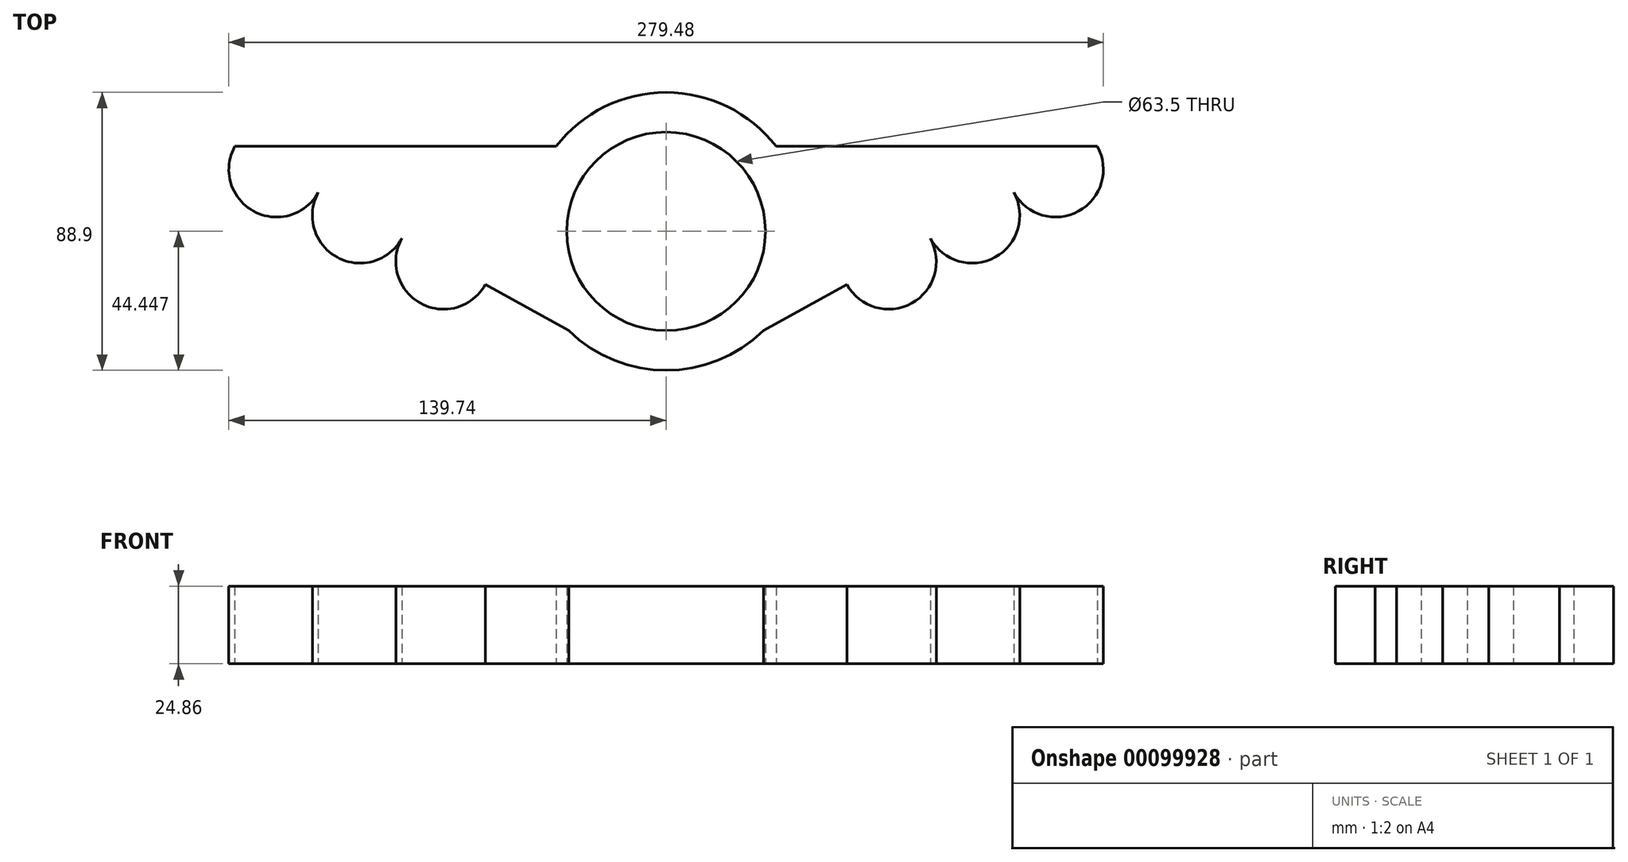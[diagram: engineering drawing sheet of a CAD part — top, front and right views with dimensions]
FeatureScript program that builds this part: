
annotation { "Feature Type Name" : "Feature", "Feature Type Description" : "" }
export const myFeature = defineFeature(function(context is Context, id is Id, definition is map)
    precondition{}
    {
        {
            var Q0;
            Q0=qCreatedBy(makeId("Top.planeOp"),FACE);
            var sketch = newSketch(context, id + "F0", { "sketchPlane" : qUnion([Q0])});
            skCircle(sketch, "E0", {"center": v(0, -31.71) * mm, "radius": 44.45 * mm});
            skCircle(sketch, "E1", {"center": v(0, -31.71) * mm, "radius": 31.75 * mm});
            skLineSegment(sketch, "E2", {"start": v(0, -31.71) * mm, "end": v(44.45, -31.71) * mm});
            skLineSegment(sketch, "E3", {"start": v(44.45, -31.71) * mm, "end": v(44.45, 0) * mm});
            skLineSegment(sketch, "E4", {"start": v(44.45, 0) * mm, "end": v(0, 0) * mm});
            skLineSegment(sketch, "E5", {"start": v(44.45, 0) * mm, "end": v(146.05, 0) * mm});
            skLineSegment(sketch, "E6", {"start": v(0, -63.46) * mm, "end": v(44.45, -63.46) * mm});
            skLineSegment(sketch, "E7", {"start": v(44.45, -31.71) * mm, "end": v(44.45, -63.46) * mm});
            skLineSegment(sketch, "E8", {"start": v(31.1, -63.46) * mm, "end": v(146.05, 0) * mm});
            skCircle(sketch, "E9", {"center": v(44.45, -56.1) * mm, "radius": 15.24 * mm});
            skCircle(sketch, "E10", {"center": v(71.13, -41.36) * mm, "radius": 15.24 * mm});
            skCircle(sketch, "E11", {"center": v(97.82, -26.63) * mm, "radius": 15.24 * mm});
            skCircle(sketch, "E12", {"center": v(124.5, -11.9) * mm, "radius": 15.24 * mm});
            skLineSegment(sketch, "E13", {"start": v(137.84, -4.53) * mm, "end": v(35.17, -4.53) * mm});
            skLineSegment(sketch, "E14", {"start": v(0, -31.71) * mm, "end": v(-44.45, -31.71) * mm});
            skLineSegment(sketch, "E15", {"start": v(0, 0) * mm, "end": v(-44.45, 0) * mm});
            skLineSegment(sketch, "E16", {"start": v(-44.45, 0) * mm, "end": v(-146.05, 0) * mm});
            skLineSegment(sketch, "E17", {"start": v(-44.45, -31.71) * mm, "end": v(-44.45, -63.46) * mm});
            skLineSegment(sketch, "E18", {"start": v(0, -63.46) * mm, "end": v(-44.45, -63.46) * mm});
            skLineSegment(sketch, "E19", {"start": v(-31.1, -63.46) * mm, "end": v(-146.05, 0) * mm});
            skCircle(sketch, "E20", {"center": v(-44.45, -56.1) * mm, "radius": 15.24 * mm});
            skCircle(sketch, "E21", {"center": v(-71.13, -41.36) * mm, "radius": 15.24 * mm});
            skCircle(sketch, "E22", {"center": v(-97.82, -26.63) * mm, "radius": 15.24 * mm});
            skCircle(sketch, "E23", {"center": v(-124.5, -11.9) * mm, "radius": 15.24 * mm});
            skLineSegment(sketch, "E24", {"start": v(-137.84, -4.53) * mm, "end": v(-35.17, -4.53) * mm});
            skSolve(sketch);
        }
        {
            var Q0;
            Q0=makeQuery(id+"F0.imprint","IMPRINT",FACE,{"disambiguationData":[TD([[makeQuery(id+"F0.imprint","IMPRINT",EDGE,{"derivedFrom":sQuery(id+"F0.wireOp",EDGE,"E0")}),1.0]])]});
            var Q1;
            {var subQ0=sQuery(id+"F0.wireOp",EDGE,"E6");var subQ5=sQuery(id+"F0.wireOp",EDGE,"E1");var subQ6=makeQuery(id+"F0.imprint","INTERSECT",VERTEX,{"derivedFrom":[subQ5,subQ0]});Q1=makeQuery(id+"F0.imprint","IMPRINT",FACE,{"disambiguationData":[TD([[makeQuery(id+"F0.imprint","IMPRINT",EDGE,{"disambiguationData":[TD([[subQ6,1.0]])],"derivedFrom":subQ5}),-1.0]])]});}
            var Q2;
            {var subQ3=sQuery(id+"F0.wireOp",EDGE,"E1");var subQ5=sQuery(id+"F0.wireOp",EDGE,"E6");var subQ6=makeQuery(id+"F0.imprint","INTERSECT",VERTEX,{"derivedFrom":[subQ3,subQ5]});Q2=makeQuery(id+"F0.imprint","IMPRINT",FACE,{"disambiguationData":[TD([[makeQuery(id+"F0.imprint","IMPRINT",EDGE,{"disambiguationData":[TD([[subQ6,-1.0]])],"derivedFrom":subQ3}),-1.0]])]});}
            var Q3;
            {var subQ0=sQuery(id+"F0.wireOp",EDGE,"E9");var subQ1=sQuery(id+"F0.wireOp",EDGE,"E0");var subQ3=makeQuery(id+"F0.imprint","INTERSECT",VERTEX,{"derivedFrom":[subQ1,subQ0]});Q3=makeQuery(id+"F0.imprint","IMPRINT",FACE,{"disambiguationData":[TD([[makeQuery(id+"F0.imprint","IMPRINT",EDGE,{"disambiguationData":[TD([[subQ3,1.0]])],"derivedFrom":subQ1}),1.0]])]});}
            var Q4;
            {var subQ0=sQuery(id+"F0.wireOp",EDGE,"E9");var subQ5=sQuery(id+"F0.wireOp",EDGE,"E7");var subQ6=makeQuery(id+"F0.imprint","INTERSECT",VERTEX,{"derivedFrom":[subQ5,subQ0]});Q4=makeQuery(id+"F0.imprint","IMPRINT",FACE,{"disambiguationData":[TD([[makeQuery(id+"F0.imprint","IMPRINT",EDGE,{"disambiguationData":[TD([[subQ6,-1.0]])],"derivedFrom":subQ5}),-1.0]])]});}
            var Q5;
            {var subQ0=sQuery(id+"F0.wireOp",EDGE,"E9");var subQ1=sQuery(id+"F0.wireOp",EDGE,"E7");var subQ2=makeQuery(id+"F0.imprint","INTERSECT",VERTEX,{"derivedFrom":[subQ1,subQ0]});Q5=makeQuery(id+"F0.imprint","IMPRINT",FACE,{"disambiguationData":[TD([[makeQuery(id+"F0.imprint","IMPRINT",EDGE,{"disambiguationData":[TD([[subQ2,-1.0]])],"derivedFrom":subQ1}),1.0]])]});}
            var Q6;
            {var subQ0=sQuery(id+"F0.wireOp",EDGE,"E10");var subQ1=sQuery(id+"F0.wireOp",EDGE,"E8");var subQ2=makeQuery(id+"F0.imprint","INTERSECT",VERTEX,{"derivedFrom":[subQ1,sQuery(id+"F0.wireOp",EDGE,"E9"),subQ0]});Q6=makeQuery(id+"F0.imprint","IMPRINT",FACE,{"disambiguationData":[TD([[makeQuery(id+"F0.imprint","IMPRINT",EDGE,{"disambiguationData":[TD([[subQ2,-1.0]])],"derivedFrom":subQ1}),1.0]])]});}
            var Q7;
            {var subQ0=sQuery(id+"F0.wireOp",EDGE,"E10");var subQ1=sQuery(id+"F0.wireOp",EDGE,"E8");var subQ2=makeQuery(id+"F0.imprint","INTERSECT",VERTEX,{"derivedFrom":[subQ1,sQuery(id+"F0.wireOp",EDGE,"E9"),subQ0]});Q7=makeQuery(id+"F0.imprint","IMPRINT",FACE,{"disambiguationData":[TD([[makeQuery(id+"F0.imprint","IMPRINT",EDGE,{"disambiguationData":[TD([[subQ2,-1.0]])],"derivedFrom":subQ1}),-1.0]])]});}
            var Q8;
            {var subQ1=sQuery(id+"F0.wireOp",EDGE,"E0");var subQ3=sQuery(id+"F0.wireOp",EDGE,"E13");var subQ4=makeQuery(id+"F0.imprint","INTERSECT",VERTEX,{"derivedFrom":[subQ1,subQ3]});Q8=makeQuery(id+"F0.imprint","IMPRINT",FACE,{"disambiguationData":[TD([[makeQuery(id+"F0.imprint","IMPRINT",EDGE,{"disambiguationData":[TD([[subQ4,1.0]])],"derivedFrom":subQ3}),1.0]])]});}
            var Q9;
            {var subQ0=sQuery(id+"F0.wireOp",EDGE,"E13");var subQ1=sQuery(id+"F0.wireOp",EDGE,"E12");var subQ5=makeQuery(id+"F0.imprint","INTERSECT",VERTEX,{"derivedFrom":[subQ1,subQ0]});Q9=makeQuery(id+"F0.imprint","IMPRINT",FACE,{"disambiguationData":[TD([[makeQuery(id+"F0.imprint","IMPRINT",EDGE,{"disambiguationData":[TD([[subQ5,-1.0]])],"derivedFrom":subQ1}),1.0]])]});}
            var Q10;
            {var subQ0=sQuery(id+"F0.wireOp",EDGE,"E12");var subQ1=sQuery(id+"F0.wireOp",EDGE,"E8");var subQ2=makeQuery(id+"F0.imprint","INTERSECT",VERTEX,{"derivedFrom":[subQ1,subQ0,sQuery(id+"F0.wireOp",EDGE,"E13")]});Q10=makeQuery(id+"F0.imprint","IMPRINT",FACE,{"disambiguationData":[TD([[makeQuery(id+"F0.imprint","IMPRINT",EDGE,{"disambiguationData":[TD([[subQ2,1.0]])],"derivedFrom":subQ1}),-1.0]])]});}
            var Q11;
            {var subQ0=sQuery(id+"F0.wireOp",EDGE,"E11");var subQ1=sQuery(id+"F0.wireOp",EDGE,"E8");var subQ2=makeQuery(id+"F0.imprint","INTERSECT",VERTEX,{"derivedFrom":[subQ1,sQuery(id+"F0.wireOp",EDGE,"E10"),subQ0]});Q11=makeQuery(id+"F0.imprint","IMPRINT",FACE,{"disambiguationData":[TD([[makeQuery(id+"F0.imprint","IMPRINT",EDGE,{"disambiguationData":[TD([[subQ2,-1.0]])],"derivedFrom":subQ1}),-1.0]])]});}
            var Q12;
            {var subQ0=sQuery(id+"F0.wireOp",EDGE,"E11");var subQ1=sQuery(id+"F0.wireOp",EDGE,"E8");var subQ2=makeQuery(id+"F0.imprint","INTERSECT",VERTEX,{"derivedFrom":[subQ1,sQuery(id+"F0.wireOp",EDGE,"E10"),subQ0]});Q12=makeQuery(id+"F0.imprint","IMPRINT",FACE,{"disambiguationData":[TD([[makeQuery(id+"F0.imprint","IMPRINT",EDGE,{"disambiguationData":[TD([[subQ2,-1.0]])],"derivedFrom":subQ1}),1.0]])]});}
            var Q13;
            {var subQ6=sQuery(id+"F0.wireOp",EDGE,"E3");var subQ8=sQuery(id+"F0.wireOp",EDGE,"E13");var subQ9=makeQuery(id+"F0.imprint","INTERSECT",VERTEX,{"derivedFrom":[subQ6,subQ8]});Q13=makeQuery(id+"F0.imprint","IMPRINT",FACE,{"disambiguationData":[TD([[makeQuery(id+"F0.imprint","IMPRINT",EDGE,{"disambiguationData":[TD([[subQ9,1.0]])],"derivedFrom":subQ8}),1.0]])]});}
            var Q14;
            {var subQ1=sQuery(id+"F0.wireOp",EDGE,"E0");var subQ3=sQuery(id+"F0.wireOp",EDGE,"E9");var subQ4=makeQuery(id+"F0.imprint","INTERSECT",VERTEX,{"derivedFrom":[subQ1,subQ3]});Q14=makeQuery(id+"F0.imprint","IMPRINT",FACE,{"disambiguationData":[TD([[makeQuery(id+"F0.imprint","IMPRINT",EDGE,{"disambiguationData":[TD([[subQ4,1.0]])],"derivedFrom":subQ3}),-1.0]])]});}
            var Q15;
            {var subQ5=sQuery(id+"F0.wireOp",EDGE,"E0");var subQ6=makeQuery(id+"F0.imprint","INTERSECT",VERTEX,{"derivedFrom":[subQ5,sQuery(id+"F0.wireOp",EDGE,"E13")]});Q15=makeQuery(id+"F0.imprint","IMPRINT",FACE,{"disambiguationData":[TD([[makeQuery(id+"F0.imprint","IMPRINT",EDGE,{"disambiguationData":[TD([[subQ6,-1.0]])],"derivedFrom":subQ5}),1.0]])]});}
            var Q16;
            {var subQ1=sQuery(id+"F0.wireOp",EDGE,"E0");var subQ8=makeQuery(id+"F0.imprint","INTERSECT",VERTEX,{"derivedFrom":[subQ1,sQuery(id+"F0.wireOp",EDGE,"E24")]});Q16=makeQuery(id+"F0.imprint","IMPRINT",FACE,{"disambiguationData":[TD([[makeQuery(id+"F0.imprint","IMPRINT",EDGE,{"disambiguationData":[TD([[subQ8,1.0]])],"derivedFrom":subQ1}),1.0]])]});}
            var Q17;
            {var subQ8=sQuery(id+"F0.wireOp",EDGE,"E0");var subQ10=sQuery(id+"F0.wireOp",EDGE,"E24");var subQ11=makeQuery(id+"F0.imprint","INTERSECT",VERTEX,{"derivedFrom":[subQ8,subQ10]});Q17=makeQuery(id+"F0.imprint","IMPRINT",FACE,{"disambiguationData":[TD([[makeQuery(id+"F0.imprint","IMPRINT",EDGE,{"disambiguationData":[TD([[subQ11,1.0]])],"derivedFrom":subQ10}),-1.0]])]});}
            var Q18;
            {var subQ0=sQuery(id+"F0.wireOp",EDGE,"E24");var subQ1=sQuery(id+"F0.wireOp",EDGE,"E23");var subQ5=makeQuery(id+"F0.imprint","INTERSECT",VERTEX,{"derivedFrom":[subQ1,subQ0]});Q18=makeQuery(id+"F0.imprint","IMPRINT",FACE,{"disambiguationData":[TD([[makeQuery(id+"F0.imprint","IMPRINT",EDGE,{"disambiguationData":[TD([[subQ5,1.0]])],"derivedFrom":subQ1}),1.0]])]});}
            var Q19;
            {var subQ0=sQuery(id+"F0.wireOp",EDGE,"E23");var subQ1=sQuery(id+"F0.wireOp",EDGE,"E19");var subQ2=makeQuery(id+"F0.imprint","INTERSECT",VERTEX,{"derivedFrom":[subQ1,subQ0,sQuery(id+"F0.wireOp",EDGE,"E24")]});Q19=makeQuery(id+"F0.imprint","IMPRINT",FACE,{"disambiguationData":[TD([[makeQuery(id+"F0.imprint","IMPRINT",EDGE,{"disambiguationData":[TD([[subQ2,1.0]])],"derivedFrom":subQ1}),1.0]])]});}
            var Q20;
            {var subQ0=sQuery(id+"F0.wireOp",EDGE,"E22");var subQ1=sQuery(id+"F0.wireOp",EDGE,"E19");var subQ2=makeQuery(id+"F0.imprint","INTERSECT",VERTEX,{"derivedFrom":[subQ1,sQuery(id+"F0.wireOp",EDGE,"E21"),subQ0]});Q20=makeQuery(id+"F0.imprint","IMPRINT",FACE,{"disambiguationData":[TD([[makeQuery(id+"F0.imprint","IMPRINT",EDGE,{"disambiguationData":[TD([[subQ2,-1.0]])],"derivedFrom":subQ1}),1.0]])]});}
            var Q21;
            {var subQ0=sQuery(id+"F0.wireOp",EDGE,"E22");var subQ1=sQuery(id+"F0.wireOp",EDGE,"E19");var subQ2=makeQuery(id+"F0.imprint","INTERSECT",VERTEX,{"derivedFrom":[subQ1,sQuery(id+"F0.wireOp",EDGE,"E21"),subQ0]});Q21=makeQuery(id+"F0.imprint","IMPRINT",FACE,{"disambiguationData":[TD([[makeQuery(id+"F0.imprint","IMPRINT",EDGE,{"disambiguationData":[TD([[subQ2,-1.0]])],"derivedFrom":subQ1}),-1.0]])]});}
            var Q22;
            {var subQ0=sQuery(id+"F0.wireOp",EDGE,"E21");var subQ1=sQuery(id+"F0.wireOp",EDGE,"E19");var subQ2=makeQuery(id+"F0.imprint","INTERSECT",VERTEX,{"derivedFrom":[subQ1,sQuery(id+"F0.wireOp",EDGE,"E20"),subQ0]});Q22=makeQuery(id+"F0.imprint","IMPRINT",FACE,{"disambiguationData":[TD([[makeQuery(id+"F0.imprint","IMPRINT",EDGE,{"disambiguationData":[TD([[subQ2,-1.0]])],"derivedFrom":subQ1}),-1.0]])]});}
            var Q23;
            {var subQ0=sQuery(id+"F0.wireOp",EDGE,"E21");var subQ1=sQuery(id+"F0.wireOp",EDGE,"E19");var subQ2=makeQuery(id+"F0.imprint","INTERSECT",VERTEX,{"derivedFrom":[subQ1,sQuery(id+"F0.wireOp",EDGE,"E20"),subQ0]});Q23=makeQuery(id+"F0.imprint","IMPRINT",FACE,{"disambiguationData":[TD([[makeQuery(id+"F0.imprint","IMPRINT",EDGE,{"disambiguationData":[TD([[subQ2,-1.0]])],"derivedFrom":subQ1}),1.0]])]});}
            var Q24;
            {var subQ1=sQuery(id+"F0.wireOp",EDGE,"E0");var subQ3=sQuery(id+"F0.wireOp",EDGE,"E20");var subQ4=makeQuery(id+"F0.imprint","INTERSECT",VERTEX,{"derivedFrom":[subQ1,subQ3]});Q24=makeQuery(id+"F0.imprint","IMPRINT",FACE,{"disambiguationData":[TD([[makeQuery(id+"F0.imprint","IMPRINT",EDGE,{"disambiguationData":[TD([[subQ4,-1.0]])],"derivedFrom":subQ3}),-1.0]])]});}
            var Q25;
            {var subQ0=sQuery(id+"F0.wireOp",EDGE,"E20");var subQ5=sQuery(id+"F0.wireOp",EDGE,"E17");var subQ6=makeQuery(id+"F0.imprint","INTERSECT",VERTEX,{"derivedFrom":[subQ5,subQ0]});Q25=makeQuery(id+"F0.imprint","IMPRINT",FACE,{"disambiguationData":[TD([[makeQuery(id+"F0.imprint","IMPRINT",EDGE,{"disambiguationData":[TD([[subQ6,-1.0]])],"derivedFrom":subQ5}),1.0]])]});}
            var Q26;
            {var subQ0=sQuery(id+"F0.wireOp",EDGE,"E20");var subQ1=sQuery(id+"F0.wireOp",EDGE,"E17");var subQ2=makeQuery(id+"F0.imprint","INTERSECT",VERTEX,{"derivedFrom":[subQ1,subQ0]});Q26=makeQuery(id+"F0.imprint","IMPRINT",FACE,{"disambiguationData":[TD([[makeQuery(id+"F0.imprint","IMPRINT",EDGE,{"disambiguationData":[TD([[subQ2,-1.0]])],"derivedFrom":subQ1}),-1.0]])]});}
            var Q27;
            {var subQ0=sQuery(id+"F0.wireOp",EDGE,"E6");var subQ3=sQuery(id+"F0.wireOp",EDGE,"E18");var subQ5=makeQuery(id+"F0.imprint","INTERSECT",VERTEX,{"derivedFrom":[sQuery(id+"F0.wireOp",EDGE,"E1"),subQ0,subQ3]});Q27=makeQuery(id+"F0.imprint","IMPRINT",FACE,{"disambiguationData":[TD([[makeQuery(id+"F0.imprint","IMPRINT",EDGE,{"disambiguationData":[TD([[subQ5,-1.0]])],"derivedFrom":subQ0}),-1.0]])]});}
            var Q28;
            {var subQ0=sQuery(id+"F0.wireOp",EDGE,"E4");var subQ1=sQuery(id+"F0.wireOp",EDGE,"E0");var subQ2=makeQuery(id+"F0.imprint","INTERSECT",VERTEX,{"derivedFrom":[subQ1,subQ0]});Q28=makeQuery(id+"F0.imprint","IMPRINT",FACE,{"disambiguationData":[TD([[makeQuery(id+"F0.imprint","IMPRINT",EDGE,{"disambiguationData":[TD([[subQ2,-1.0]])],"derivedFrom":subQ1}),1.0]])]});}
            extrude(context, id + "F1", {"entities" : qUnion([Q0, Q1, Q2, Q3, Q4, Q5, Q6, Q7, Q8, Q9, Q10, Q11, Q12, Q13, Q14, Q15, Q16, Q17, Q18, Q19, Q20, Q21, Q22, Q23, Q24, Q25, Q26, Q27, Q28]), "depth" : 24.86 * mm});
        }
    });
